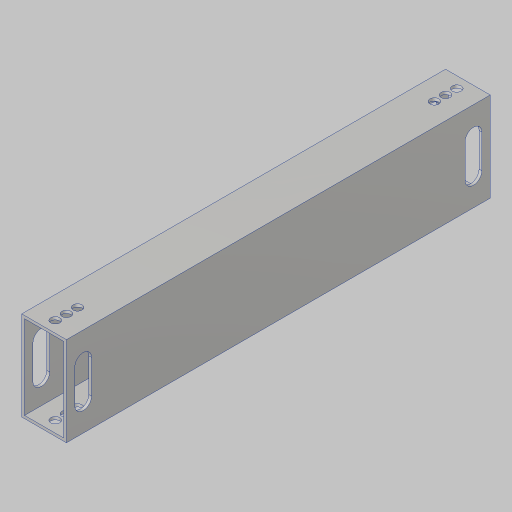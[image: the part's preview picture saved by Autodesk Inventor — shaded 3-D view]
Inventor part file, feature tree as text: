
AUTODESK INVENTOR PART (.ipt)
format: ipt  version: 2023.5 (Build 275446000, 446)  size: 154,624 bytes
history: native  units: in
note: dims shown in document units (in); Inventor stores cm internally (conversion verified against a paired STEP export)
features: extrude x2, sketch x2, hole x1
ambient origin geometry x8: Origin, YZ Plane, XZ Plane, XY Plane, X Axis, Y Axis, Z Axis, Center Point
bodies: Solid1 (feature_tree)
feature tree (5):
  extrude  "Extrusion1"  Depth=0.25in
  hole  "Hole2"  [1 undecoded]
  extrude  "Extrusion2"  Depth=0.375in
  sketch  "Sketch3"  dims[d4=0.0in d18=0.25in]
  sketch  "Sketch4"  dims[d19=0.25in d20=0.25in d21=0.5in d22=0.25in d23=0.25in d24=0.25in d25=0.201in d26=0.75in d27=0.385in d28=0.25in d29=0.5635in d30=1.0in d31=0.8108in d32=0.375in d33=0.75in d34=0.375in d35=0.0in d36=0.0in]
note: 1 required parameter value undecoded (feature->parameter linkage not recoverable at this tier; creation-order binding heuristic only, values carry confidence <= 0.55)
